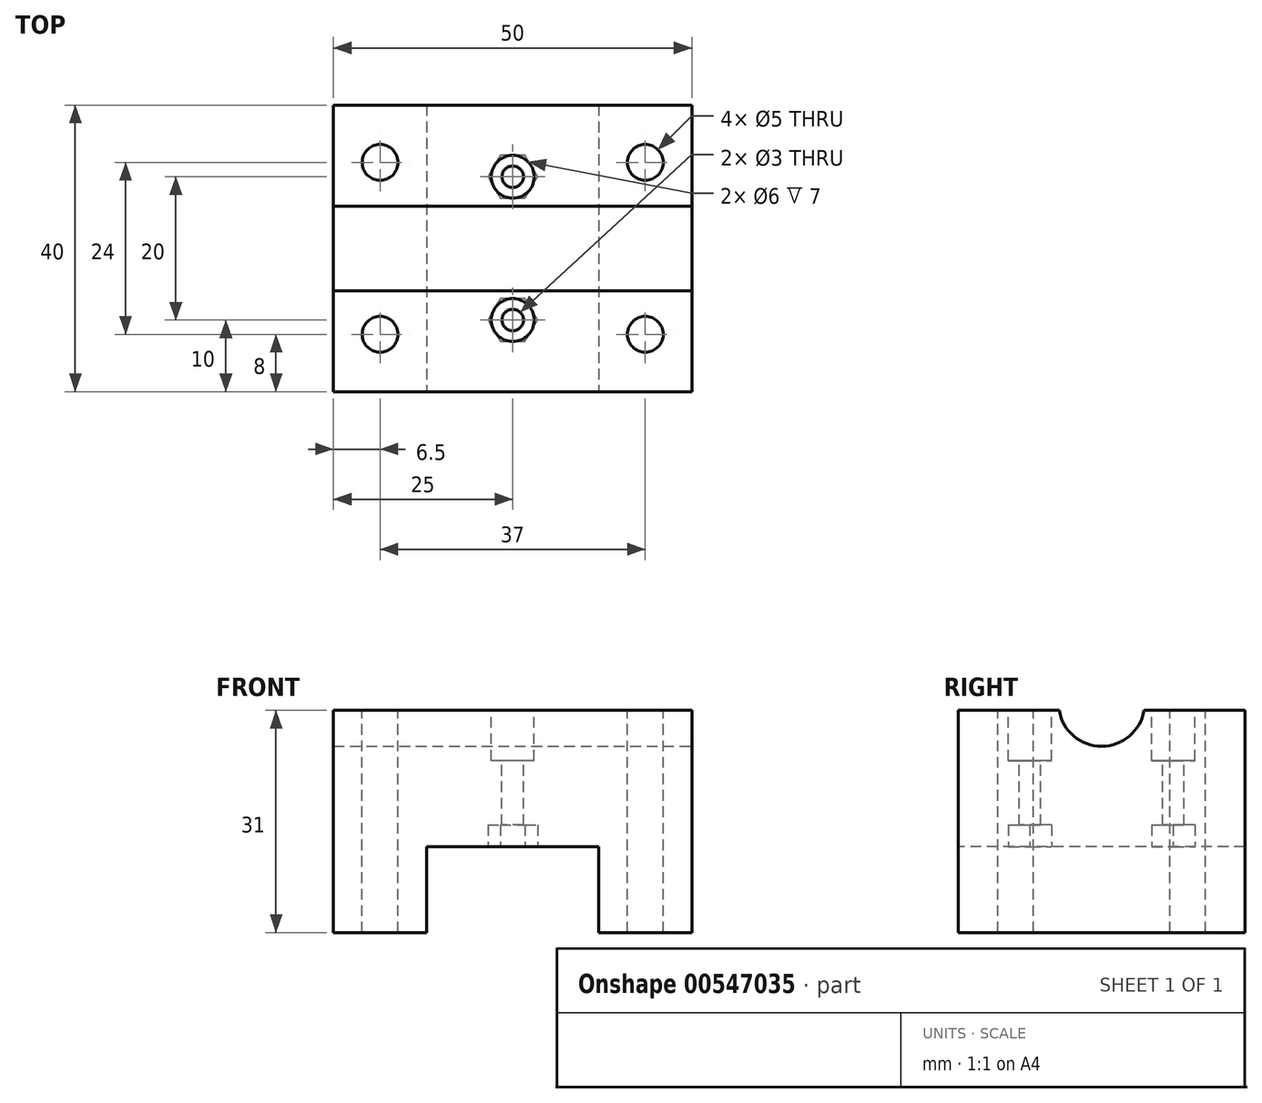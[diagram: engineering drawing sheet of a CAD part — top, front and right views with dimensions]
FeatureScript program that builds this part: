
annotation { "Feature Type Name" : "Feature", "Feature Type Description" : "" }
export const myFeature = defineFeature(function(context is Context, id is Id, definition is map)
    precondition{}
    {
        {
            var Q0;
            Q0=qCreatedBy(makeId("Top.planeOp"),FACE);
            var sketch = newSketch(context, id + "F0", { "sketchPlane" : qUnion([Q0])});
            skLineSegment(sketch, "E0.bottom", {"start": v(-50, 0) * mm, "end": v(0, 0) * mm});
            skLineSegment(sketch, "E0.top", {"start": v(-50, -40) * mm, "end": v(0, -40) * mm});
            skLineSegment(sketch, "E0.left", {"start": v(-50, 0) * mm, "end": v(-50, -40) * mm});
            skLineSegment(sketch, "E0.right", {"start": v(0, 0) * mm, "end": v(0, -40) * mm});
            skLineSegment(sketch, "E1", {"start": v(-13, 0) * mm, "end": v(-13, -40) * mm});
            skLineSegment(sketch, "E2", {"start": v(-37, 0) * mm, "end": v(-37, -40) * mm});
            skSolve(sketch);
        }
        {
            var Q0;
            Q0=makeQuery(id+"F0.imprint","IMPRINT",FACE,{"disambiguationData":[TD([[makeQuery(id+"F0.imprint","IMPRINT",EDGE,{"derivedFrom":sQuery(id+"F0.wireOp",EDGE,"E0.bottom")}),-1.0]])]});
            extrude(context, id + "F1", {"entities" : qUnion([Q0]), "depth" : 19 * mm, "offsetDistance" : 25 * mm});
        }
        {
            var Q0;
            Q0=makeQuery(id+"F1.opExtrude","SWEPT_FACE",FACE,{"disambiguationData":[OSD([sQuery(id+"F0.wireOp",EDGE,"E0.right")])]});
            var sketch = newSketch(context, id + "F2", { "sketchPlane" : qUnion([Q0])});
            skCircle(sketch, "E3", {"center": v(-20, 20) * mm, "radius": 6 * mm});
            skSolve(sketch);
        }
        {
            var Q0;
            {var subQ0=sQuery(id+"F2.wireOp",EDGE,"E3");var subQ1=makeQuery(id+"F1.opExtrude","CAP_EDGE",EDGE,{"disambiguationData":[OSD([sQuery(id+"F0.wireOp",EDGE,"E0.right")])],"isStart":false});var subQ2=makeQuery(id+"F2.imprint","INTERSECT",VERTEX,{"disambiguationData":[OD(0.0)],"derivedFrom":[subQ1,subQ0]});Q0=makeQuery(id+"F2.imprint","IMPRINT",FACE,{"disambiguationData":[TD([[makeQuery(id+"F2.imprint","IMPRINT",EDGE,{"disambiguationData":[TD([[subQ2,1.0]])],"derivedFrom":subQ0}),1.0]])]});}
            extrude(context, id + "F3", {"entities" : qUnion([Q0]), "operationType" : NewBodyOperationType.REMOVE, "oppositeDirection" : true, "depth" : 50 * mm, "offsetDistance" : 25 * mm});
        }
        {
            var Q0;
            {var subQ0=sQuery(id+"F0.wireOp",EDGE,"E0.right");Q0=makeQuery(id+"F0.imprint","IMPRINT",FACE,{"disambiguationData":[TD([[makeQuery(id+"F0.imprint","IMPRINT",EDGE,{"derivedFrom":subQ0}),-1.0]])]});}
            var Q1;
            {var subQ0=sQuery(id+"F0.wireOp",EDGE,"E0.left");Q1=makeQuery(id+"F0.imprint","IMPRINT",FACE,{"disambiguationData":[TD([[makeQuery(id+"F0.imprint","IMPRINT",EDGE,{"derivedFrom":subQ0}),1.0]])]});}
            extrude(context, id + "F4", {"entities" : qUnion([Q0, Q1]), "operationType" : NewBodyOperationType.ADD, "oppositeDirection" : true, "depth" : 12 * mm, "offsetDistance" : 25 * mm});
        }
        {
            var Q0;
            {var subQ0=sQuery(id+"F0.wireOp",EDGE,"E0.bottom");var subQ1=sQuery(id+"F0.wireOp",EDGE,"E0.right");var subQ2=sQuery(id+"F0.wireOp",EDGE,"E0.top");Q0=makeQuery(id+"F3.boolean.opBoolean","SPLIT",FACE,{"disambiguationData":[TD([makeQuery(id+"F1.opExtrude","SWEPT_FACE",FACE,{"disambiguationData":[OSD([subQ1])]})])],"derivedFrom":makeQuery(id+"F1.opExtrude","CAP_FACE",FACE,{"disambiguationData":[OSD([subQ0,subQ2,sQuery(id+"F0.wireOp",EDGE,"E0.left"),subQ1])],"isStart":false})});}
            var sketch = newSketch(context, id + "F5", { "sketchPlane" : qUnion([Q0])});
            skPoint(sketch, "E4", {"position": v(-6.5, -8) * mm});
            skPoint(sketch, "E5", {"position": v(-43.5, -8) * mm});
            skPoint(sketch, "E6", {"position": v(-6.5, -32) * mm});
            skPoint(sketch, "E7", {"position": v(-43.5, -32) * mm});
            skSolve(sketch);
        }
        {
            var Q0;
            Q0=sQuery(id+"F5.wireOp",VERTEX,"E6");
            var Q1;
            Q1=sQuery(id+"F5.wireOp",VERTEX,"E7");
            var Q2;
            Q2=sQuery(id+"F5.wireOp",VERTEX,"E5");
            var Q3;
            Q3=sQuery(id+"F5.wireOp",VERTEX,"E4");
            var Q4;
            Q4=makeQuery(id+"F1.opExtrude","SWEPT_BODY",BODY,{"disambiguationData":[OSD([sQuery(id+"F0.wireOp",EDGE,"E0.bottom"),sQuery(id+"F0.wireOp",EDGE,"E0.top"),sQuery(id+"F0.wireOp",EDGE,"E0.left"),sQuery(id+"F0.wireOp",EDGE,"E0.right")])]});
            hole(context, id + "F6", {"style" : HoleStyle.SIMPLE, "endStyle" : HoleEndStyle.THROUGH, "holeDiameter" : 5 * mm, "isTappedThrough" : true, "tappedDepth" : 12 * mm, "tapClearance" : 3, "startFromSketch" : true, "locations" : qUnion([Q0, Q1, Q2, Q3]), "scope" : qUnion([Q4])});
        }
        {
            var Q0;
            {var subQ0=sQuery(id+"F0.wireOp",EDGE,"E0.bottom");var subQ1=sQuery(id+"F0.wireOp",EDGE,"E0.right");var subQ2=sQuery(id+"F0.wireOp",EDGE,"E0.top");Q0=makeQuery(id+"F3.boolean.opBoolean","SPLIT",FACE,{"disambiguationData":[TD([makeQuery(id+"F1.opExtrude","SWEPT_FACE",FACE,{"disambiguationData":[OSD([subQ1])]})])],"derivedFrom":makeQuery(id+"F1.opExtrude","CAP_FACE",FACE,{"disambiguationData":[OSD([subQ0,subQ2,sQuery(id+"F0.wireOp",EDGE,"E0.left"),subQ1])],"isStart":false})});}
            var sketch = newSketch(context, id + "F7", { "sketchPlane" : qUnion([Q0])});
            skPoint(sketch, "E8", {"position": v(-25, -10) * mm});
            skPoint(sketch, "E9", {"position": v(-25, -30) * mm});
            skSolve(sketch);
        }
        {
            var Q0;
            Q0=sQuery(id+"F7.wireOp",VERTEX,"E8");
            var Q1;
            Q1=sQuery(id+"F7.wireOp",VERTEX,"E9");
            var Q2;
            Q2=makeQuery(id+"F1.opExtrude","SWEPT_BODY",BODY,{"disambiguationData":[OSD([sQuery(id+"F0.wireOp",EDGE,"E0.bottom"),sQuery(id+"F0.wireOp",EDGE,"E0.top"),sQuery(id+"F0.wireOp",EDGE,"E0.left"),sQuery(id+"F0.wireOp",EDGE,"E0.right")])]});
            hole(context, id + "F8", {"style" : HoleStyle.C_BORE, "endStyle" : HoleEndStyle.THROUGH, "holeDiameter" : 3 * mm, "cBoreDiameter" : 6 * mm, "cBoreDepth" : 7 * mm, "isTappedThrough" : true, "tappedDepth" : 12 * mm, "tapClearance" : 3, "startFromSketch" : true, "locations" : qUnion([Q0, Q1]), "scope" : qUnion([Q2])});
        }
        {
            var Q0;
            Q0=makeQuery(id+"F1.opExtrude","CAP_FACE",FACE,{"disambiguationData":[OSD([sQuery(id+"F0.wireOp",EDGE,"E0.bottom"),sQuery(id+"F0.wireOp",EDGE,"E0.top"),sQuery(id+"F0.wireOp",EDGE,"E0.left"),sQuery(id+"F0.wireOp",EDGE,"E0.right")])],"isStart":true});
            var sketch = newSketch(context, id + "F9", { "sketchPlane" : qUnion([Q0])});
            skLineSegment(sketch, "E10", {"start": v(-26.73, 13) * mm, "end": v(-23.27, 13) * mm});
            skLineSegment(sketch, "E11", {"start": v(-23.27, 13) * mm, "end": v(-21.54, 10) * mm});
            skLineSegment(sketch, "E12", {"start": v(-21.54, 10) * mm, "end": v(-23.27, 7) * mm});
            skLineSegment(sketch, "E13", {"start": v(-23.27, 7) * mm, "end": v(-26.73, 7) * mm});
            skLineSegment(sketch, "E14", {"start": v(-26.73, 7) * mm, "end": v(-28.46, 10) * mm});
            skLineSegment(sketch, "E15", {"start": v(-28.46, 10) * mm, "end": v(-26.73, 13) * mm});
            skCircle(sketch, "E16", {"center": v(-25, 10) * mm, "radius": 3.46 * mm});
            skLineSegment(sketch, "E17", {"start": v(-26.73, 33) * mm, "end": v(-23.27, 33) * mm});
            skLineSegment(sketch, "E18", {"start": v(-23.27, 33) * mm, "end": v(-21.54, 30) * mm});
            skLineSegment(sketch, "E19", {"start": v(-21.54, 30) * mm, "end": v(-23.27, 27) * mm});
            skLineSegment(sketch, "E20", {"start": v(-23.27, 27) * mm, "end": v(-26.73, 27) * mm});
            skLineSegment(sketch, "E21", {"start": v(-26.73, 27) * mm, "end": v(-28.46, 30) * mm});
            skLineSegment(sketch, "E22", {"start": v(-28.46, 30) * mm, "end": v(-26.73, 33) * mm});
            skCircle(sketch, "E23", {"center": v(-25, 30) * mm, "radius": 3.46 * mm});
            skSolve(sketch);
        }
        {
            var Q0;
            Q0=makeQuery(id+"F9.imprint","IMPRINT",FACE,{"disambiguationData":[TD([[makeQuery(id+"F9.imprint","IMPRINT",EDGE,{"derivedFrom":sQuery(id+"F9.wireOp",EDGE,"E10")}),-1.0]])]});
            var Q1;
            Q1=makeQuery(id+"F9.imprint","IMPRINT",FACE,{"disambiguationData":[TD([[makeQuery(id+"F9.imprint","IMPRINT",EDGE,{"derivedFrom":sQuery(id+"F9.wireOp",EDGE,"E17")}),-1.0]])]});
            extrude(context, id + "F10", {"entities" : qUnion([Q0, Q1]), "operationType" : NewBodyOperationType.REMOVE, "oppositeDirection" : true, "depth" : 3 * mm, "offsetDistance" : 25 * mm});
        }
    });
